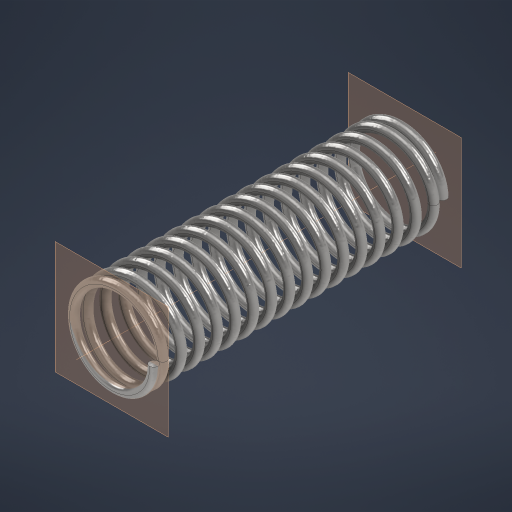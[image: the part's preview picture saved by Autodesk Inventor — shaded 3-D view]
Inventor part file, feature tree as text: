
AUTODESK INVENTOR PART (.ipt)
format: ipt  version: 2024 (Build 280153000, 153)  size: 1,240,064 bytes
history: native  units: in
note: dims shown in document units (in); Inventor stores cm internally (conversion verified against a paired STEP export)
features: plane x1, sweep x1
ambient origin geometry x8: Origin, YZ Plane, XZ Plane, XY Plane, X Axis, Y Axis, Z Axis, Center Point
bodies: Solid1 (feature_tree)
feature tree (2):
  plane  "Work Plane1"
  sweep  "Sweep1"
